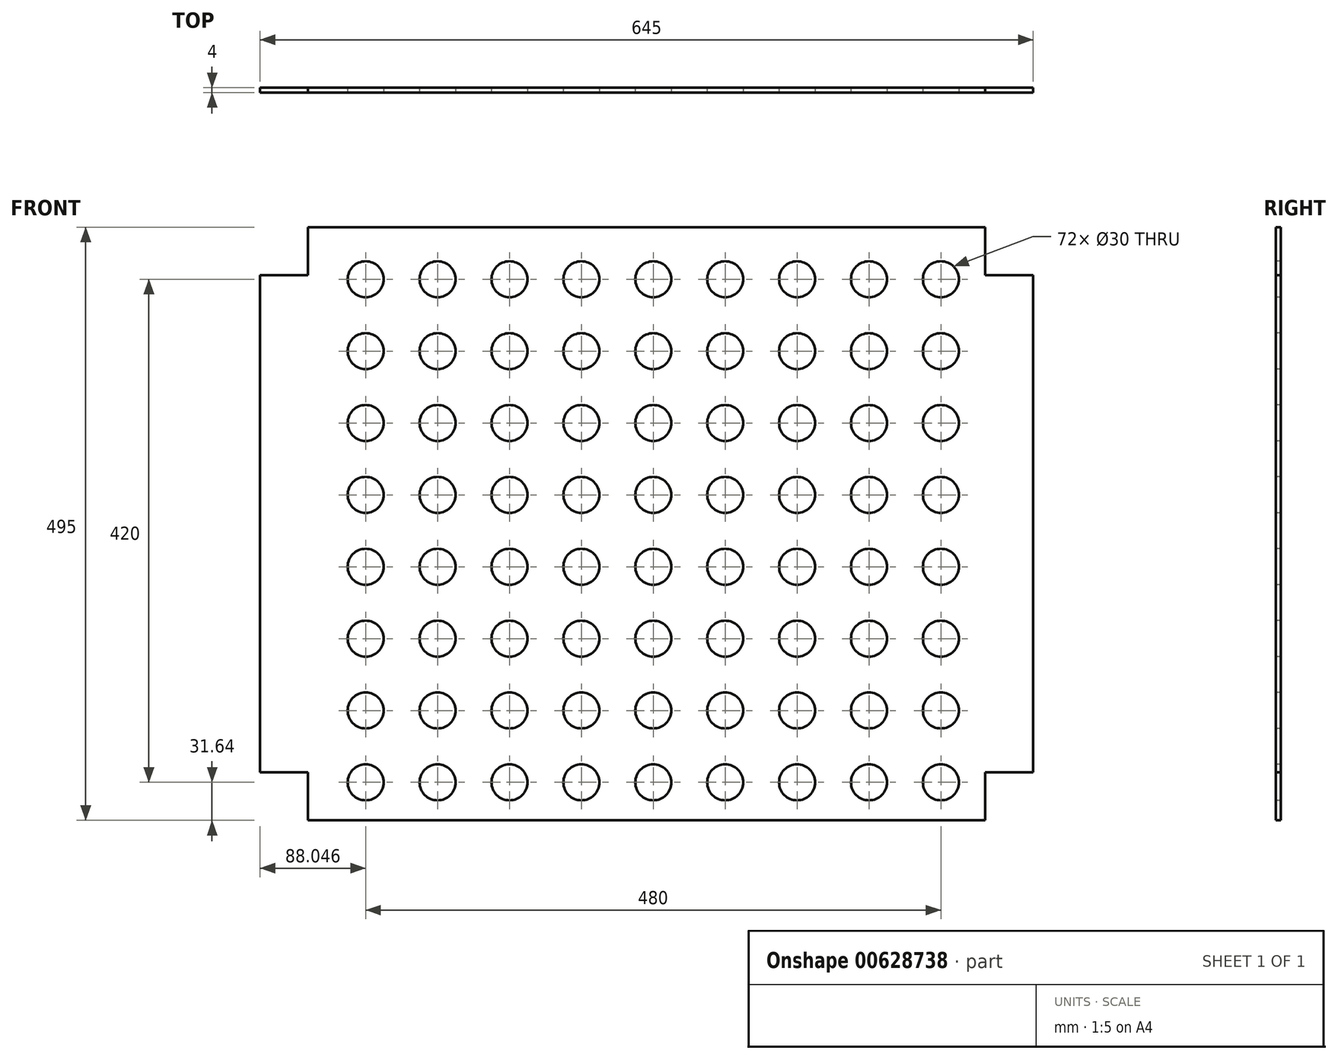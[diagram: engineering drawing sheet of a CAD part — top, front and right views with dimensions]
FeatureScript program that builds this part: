
annotation { "Feature Type Name" : "Feature", "Feature Type Description" : "" }
export const myFeature = defineFeature(function(context is Context, id is Id, definition is map)
    precondition{}
    {
        {
            var Q0;
            Q0=qCreatedBy(makeId("Front.planeOp"),FACE);
            var sketch = newSketch(context, id + "F0", { "sketchPlane" : qUnion([Q0])});
            skLineSegment(sketch, "E0", {"start": v(0, 247.5) * mm, "end": v(-282.5, 247.5) * mm});
            skLineSegment(sketch, "E1", {"start": v(-282.5, 247.5) * mm, "end": v(-282.5, 207.5) * mm});
            skLineSegment(sketch, "E2", {"start": v(-282.5, 207.5) * mm, "end": v(-322.5, 207.5) * mm});
            skLineSegment(sketch, "E3", {"start": v(-322.5, 207.5) * mm, "end": v(-322.5, 0) * mm});
            skLineSegment(sketch, "E4.MirrorCS", {"start": v(0, 247.5) * mm, "end": v(282.5, 247.5) * mm});
            skLineSegment(sketch, "E5.MirrorCS", {"start": v(282.5, 247.5) * mm, "end": v(282.5, 207.5) * mm});
            skLineSegment(sketch, "E6.MirrorCS", {"start": v(282.5, 207.5) * mm, "end": v(322.5, 207.5) * mm});
            skLineSegment(sketch, "E7.MirrorCS", {"start": v(322.5, 207.5) * mm, "end": v(322.5, 0) * mm});
            skLineSegment(sketch, "E8.MirrorCS", {"start": v(-322.5, -207.5) * mm, "end": v(-322.5, 0) * mm});
            skLineSegment(sketch, "E9.MirrorCS", {"start": v(-282.5, -207.5) * mm, "end": v(-322.5, -207.5) * mm});
            skLineSegment(sketch, "E10.MirrorCS", {"start": v(-282.5, -247.5) * mm, "end": v(-282.5, -207.5) * mm});
            skLineSegment(sketch, "E11.MirrorCS", {"start": v(0, -247.5) * mm, "end": v(-282.5, -247.5) * mm});
            skLineSegment(sketch, "E12.MirrorCS", {"start": v(0, -247.5) * mm, "end": v(282.5, -247.5) * mm});
            skLineSegment(sketch, "E13.MirrorCS", {"start": v(282.5, -247.5) * mm, "end": v(282.5, -207.5) * mm});
            skLineSegment(sketch, "E14.MirrorCS", {"start": v(282.5, -207.5) * mm, "end": v(322.5, -207.5) * mm});
            skLineSegment(sketch, "E15.MirrorCS", {"start": v(322.5, -207.5) * mm, "end": v(322.5, 0) * mm});
            skSolve(sketch);
        }
        {
            var Q0;
            Q0=makeQuery(id+"F0.imprint","IMPRINT",FACE,{"disambiguationData":[TD([[makeQuery(id+"F0.imprint","IMPRINT",EDGE,{"derivedFrom":sQuery(id+"F0.wireOp",EDGE,"E0")}),1.0]])]});
            extrude(context, id + "F1", {"entities" : qUnion([Q0]), "depth" : 4 * mm, "offsetDistance" : 25.4 * mm});
        }
        {
            var Q0;
            Q0=makeQuery(id+"F1.opExtrude","CAP_FACE",FACE,{"disambiguationData":[OSD([sQuery(id+"F0.wireOp",EDGE,"E0"),sQuery(id+"F0.wireOp",EDGE,"E1"),sQuery(id+"F0.wireOp",EDGE,"E2"),sQuery(id+"F0.wireOp",EDGE,"E3"),sQuery(id+"F0.wireOp",EDGE,"E4.MirrorCS"),sQuery(id+"F0.wireOp",EDGE,"E5.MirrorCS"),sQuery(id+"F0.wireOp",EDGE,"E6.MirrorCS"),sQuery(id+"F0.wireOp",EDGE,"E7.MirrorCS"),sQuery(id+"F0.wireOp",EDGE,"E8.MirrorCS"),sQuery(id+"F0.wireOp",EDGE,"E9.MirrorCS"),sQuery(id+"F0.wireOp",EDGE,"E10.MirrorCS"),sQuery(id+"F0.wireOp",EDGE,"E11.MirrorCS"),sQuery(id+"F0.wireOp",EDGE,"E12.MirrorCS"),sQuery(id+"F0.wireOp",EDGE,"E13.MirrorCS"),sQuery(id+"F0.wireOp",EDGE,"E14.MirrorCS"),sQuery(id+"F0.wireOp",EDGE,"E15.MirrorCS")])],"isStart":false});
            var sketch = newSketch(context, id + "F2", { "sketchPlane" : qUnion([Q0])});
            skCircle(sketch, "E16", {"center": v(245.55, -215.86) * mm, "radius": 15 * mm});
            skCircle(sketch, "E17.0.1.0", {"center": v(245.55, -155.86) * mm, "radius": 15 * mm});
            skCircle(sketch, "E17.0.2.0", {"center": v(245.55, -95.86) * mm, "radius": 15 * mm});
            skCircle(sketch, "E17.0.3.0", {"center": v(245.55, -35.86) * mm, "radius": 15 * mm});
            skCircle(sketch, "E17.0.4.0", {"center": v(245.55, 24.14) * mm, "radius": 15 * mm});
            skCircle(sketch, "E17.0.5.0", {"center": v(245.55, 84.14) * mm, "radius": 15 * mm});
            skCircle(sketch, "E17.0.6.0", {"center": v(245.55, 144.14) * mm, "radius": 15 * mm});
            skCircle(sketch, "E17.0.7.0", {"center": v(245.55, 204.14) * mm, "radius": 15 * mm});
            skCircle(sketch, "E17.1.0.0", {"center": v(185.55, -215.86) * mm, "radius": 15 * mm});
            skCircle(sketch, "E17.1.1.0", {"center": v(185.55, -155.86) * mm, "radius": 15 * mm});
            skCircle(sketch, "E17.1.2.0", {"center": v(185.55, -95.86) * mm, "radius": 15 * mm});
            skCircle(sketch, "E17.1.3.0", {"center": v(185.55, -35.86) * mm, "radius": 15 * mm});
            skCircle(sketch, "E17.1.4.0", {"center": v(185.55, 24.14) * mm, "radius": 15 * mm});
            skCircle(sketch, "E17.1.5.0", {"center": v(185.55, 84.14) * mm, "radius": 15 * mm});
            skCircle(sketch, "E17.1.6.0", {"center": v(185.55, 144.14) * mm, "radius": 15 * mm});
            skCircle(sketch, "E17.1.7.0", {"center": v(185.55, 204.14) * mm, "radius": 15 * mm});
            skCircle(sketch, "E17.2.0.0", {"center": v(125.55, -215.86) * mm, "radius": 15 * mm});
            skCircle(sketch, "E17.2.1.0", {"center": v(125.55, -155.86) * mm, "radius": 15 * mm});
            skCircle(sketch, "E17.2.2.0", {"center": v(125.55, -95.86) * mm, "radius": 15 * mm});
            skCircle(sketch, "E17.2.3.0", {"center": v(125.55, -35.86) * mm, "radius": 15 * mm});
            skCircle(sketch, "E17.2.4.0", {"center": v(125.55, 24.14) * mm, "radius": 15 * mm});
            skCircle(sketch, "E17.2.5.0", {"center": v(125.55, 84.14) * mm, "radius": 15 * mm});
            skCircle(sketch, "E17.2.6.0", {"center": v(125.55, 144.14) * mm, "radius": 15 * mm});
            skCircle(sketch, "E17.2.7.0", {"center": v(125.55, 204.14) * mm, "radius": 15 * mm});
            skCircle(sketch, "E17.3.0.0", {"center": v(65.55, -215.86) * mm, "radius": 15 * mm});
            skCircle(sketch, "E17.3.1.0", {"center": v(65.55, -155.86) * mm, "radius": 15 * mm});
            skCircle(sketch, "E17.3.2.0", {"center": v(65.55, -95.86) * mm, "radius": 15 * mm});
            skCircle(sketch, "E17.3.3.0", {"center": v(65.55, -35.86) * mm, "radius": 15 * mm});
            skCircle(sketch, "E17.3.4.0", {"center": v(65.55, 24.14) * mm, "radius": 15 * mm});
            skCircle(sketch, "E17.3.5.0", {"center": v(65.55, 84.14) * mm, "radius": 15 * mm});
            skCircle(sketch, "E17.3.6.0", {"center": v(65.55, 144.14) * mm, "radius": 15 * mm});
            skCircle(sketch, "E17.3.7.0", {"center": v(65.55, 204.14) * mm, "radius": 15 * mm});
            skCircle(sketch, "E17.4.0.0", {"center": v(5.55, -215.86) * mm, "radius": 15 * mm});
            skCircle(sketch, "E17.4.1.0", {"center": v(5.55, -155.86) * mm, "radius": 15 * mm});
            skCircle(sketch, "E17.4.2.0", {"center": v(5.55, -95.86) * mm, "radius": 15 * mm});
            skCircle(sketch, "E17.4.3.0", {"center": v(5.55, -35.86) * mm, "radius": 15 * mm});
            skCircle(sketch, "E17.4.4.0", {"center": v(5.55, 24.14) * mm, "radius": 15 * mm});
            skCircle(sketch, "E17.4.5.0", {"center": v(5.55, 84.14) * mm, "radius": 15 * mm});
            skCircle(sketch, "E17.4.6.0", {"center": v(5.55, 144.14) * mm, "radius": 15 * mm});
            skCircle(sketch, "E17.4.7.0", {"center": v(5.55, 204.14) * mm, "radius": 15 * mm});
            skCircle(sketch, "E17.5.0.0", {"center": v(-54.45, -215.86) * mm, "radius": 15 * mm});
            skCircle(sketch, "E17.5.1.0", {"center": v(-54.45, -155.86) * mm, "radius": 15 * mm});
            skCircle(sketch, "E17.5.2.0", {"center": v(-54.45, -95.86) * mm, "radius": 15 * mm});
            skCircle(sketch, "E17.5.3.0", {"center": v(-54.45, -35.86) * mm, "radius": 15 * mm});
            skCircle(sketch, "E17.5.4.0", {"center": v(-54.45, 24.14) * mm, "radius": 15 * mm});
            skCircle(sketch, "E17.5.5.0", {"center": v(-54.45, 84.14) * mm, "radius": 15 * mm});
            skCircle(sketch, "E17.5.6.0", {"center": v(-54.45, 144.14) * mm, "radius": 15 * mm});
            skCircle(sketch, "E17.5.7.0", {"center": v(-54.45, 204.14) * mm, "radius": 15 * mm});
            skCircle(sketch, "E17.6.0.0", {"center": v(-114.45, -215.86) * mm, "radius": 15 * mm});
            skCircle(sketch, "E17.6.1.0", {"center": v(-114.45, -155.86) * mm, "radius": 15 * mm});
            skCircle(sketch, "E17.6.2.0", {"center": v(-114.45, -95.86) * mm, "radius": 15 * mm});
            skCircle(sketch, "E17.6.3.0", {"center": v(-114.45, -35.86) * mm, "radius": 15 * mm});
            skCircle(sketch, "E17.6.4.0", {"center": v(-114.45, 24.14) * mm, "radius": 15 * mm});
            skCircle(sketch, "E17.6.5.0", {"center": v(-114.45, 84.14) * mm, "radius": 15 * mm});
            skCircle(sketch, "E17.6.6.0", {"center": v(-114.45, 144.14) * mm, "radius": 15 * mm});
            skCircle(sketch, "E17.6.7.0", {"center": v(-114.45, 204.14) * mm, "radius": 15 * mm});
            skCircle(sketch, "E17.7.0.0", {"center": v(-174.45, -215.86) * mm, "radius": 15 * mm});
            skCircle(sketch, "E17.7.1.0", {"center": v(-174.45, -155.86) * mm, "radius": 15 * mm});
            skCircle(sketch, "E17.7.2.0", {"center": v(-174.45, -95.86) * mm, "radius": 15 * mm});
            skCircle(sketch, "E17.7.3.0", {"center": v(-174.45, -35.86) * mm, "radius": 15 * mm});
            skCircle(sketch, "E17.7.4.0", {"center": v(-174.45, 24.14) * mm, "radius": 15 * mm});
            skCircle(sketch, "E17.7.5.0", {"center": v(-174.45, 84.14) * mm, "radius": 15 * mm});
            skCircle(sketch, "E17.7.6.0", {"center": v(-174.45, 144.14) * mm, "radius": 15 * mm});
            skCircle(sketch, "E17.7.7.0", {"center": v(-174.45, 204.14) * mm, "radius": 15 * mm});
            skCircle(sketch, "E17.8.0.0", {"center": v(-234.45, -215.86) * mm, "radius": 15 * mm});
            skCircle(sketch, "E17.8.1.0", {"center": v(-234.45, -155.86) * mm, "radius": 15 * mm});
            skCircle(sketch, "E17.8.2.0", {"center": v(-234.45, -95.86) * mm, "radius": 15 * mm});
            skCircle(sketch, "E17.8.3.0", {"center": v(-234.45, -35.86) * mm, "radius": 15 * mm});
            skCircle(sketch, "E17.8.4.0", {"center": v(-234.45, 24.14) * mm, "radius": 15 * mm});
            skCircle(sketch, "E17.8.5.0", {"center": v(-234.45, 84.14) * mm, "radius": 15 * mm});
            skCircle(sketch, "E17.8.6.0", {"center": v(-234.45, 144.14) * mm, "radius": 15 * mm});
            skCircle(sketch, "E17.8.7.0", {"center": v(-234.45, 204.14) * mm, "radius": 15 * mm});
            skLineSegment(sketch, "E17.direction1", {"start": v(245.55, -215.86) * mm, "end": v(185.55, -215.86) * mm, "construction": true});
            skLineSegment(sketch, "E17.direction2", {"start": v(245.55, -215.86) * mm, "end": v(245.55, -155.86) * mm, "construction": true});
            skSolve(sketch);
        }
        {
            var Q0;
            Q0=qSketchRegion(id+"F2",true);
            extrude(context, id + "F3", {"entities" : qUnion([Q0]), "operationType" : NewBodyOperationType.REMOVE, "oppositeDirection" : true, "depth" : 5 * mm, "offsetDistance" : 25.4 * mm});
        }
    });
